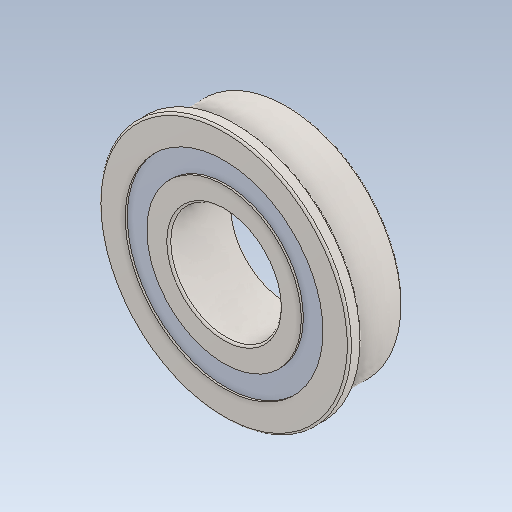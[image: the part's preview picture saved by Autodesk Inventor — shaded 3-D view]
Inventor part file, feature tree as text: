
AUTODESK INVENTOR PART (.ipt)
format: ipt  version: 2020 (Build 240168000, 168)  size: 207,872 bytes
history: native  units: in
note: dims shown in document units (in); Inventor stores cm internally (conversion verified against a paired STEP export)
features: fillet x1
ambient origin geometry x8: Origin, YZ Plane, XZ Plane, XY Plane, X Axis, Y Axis, Z Axis, Center Point
bodies: Solid1 (feature_tree)
feature tree (1):
  fillet  "Fillet1"  [1 undecoded]
note: 1 required parameter value undecoded (feature->parameter linkage not recoverable at this tier; creation-order binding heuristic only, values carry confidence <= 0.55)
